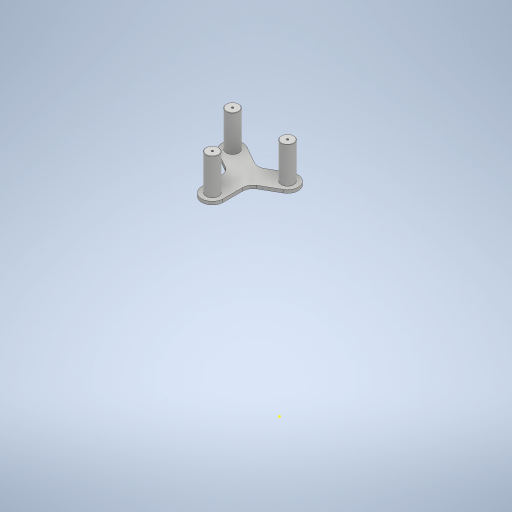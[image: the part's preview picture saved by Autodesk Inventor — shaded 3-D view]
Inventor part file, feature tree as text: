
AUTODESK INVENTOR PART (.ipt)
format: ipt  version: 2023 (Build 270158000, 158)  size: 316,416 bytes
history: native  units: mm
features: extrude x3, sketch x3, hole x3, plane x2, fillet x1
ambient origin geometry x8: Origin, YZ Plane, XZ Plane, XY Plane, X Axis, Y Axis, Z Axis, Center Point
bodies: 实体1 (feature_tree)
feature tree (12):
  plane  "工作平面5"
  extrude  "拉伸1"  Depth=12.0mm
  plane  "工作平面2"
  sketch  "草图9"  dims[d37=20.0mm d38=20.0mm]
  extrude  "拉伸3"  Depth=20.0mm
  hole  "孔4"  [1 undecoded]
  hole  "孔5"  [1 undecoded]
  hole  "孔6"  [1 undecoded]
  fillet  "圆角4"  Radius=37.0mm
  extrude  "拉伸4"  Depth=10.0mm
  sketch  "草图5"  dims[d31=12.0mm d33=12.0mm]
  sketch  "草图10"  dims[d39=15.0mm d44=10.0mm d45=3.0mm d46=0.0mm d87=12.0mm d88=37.0mm d91=0.0mm d101=10.0mm d102=10.0mm d94=1.941mm d95=5.029mm d96=4.0mm d97=2.0mm d98=90.0deg d99=10.0mm d100=20.594885mm d103=10.0mm d104=10.0mm d105=1.941mm d106=5.029mm d107=4.0mm d108=2.0mm d109=90.0deg d110=10.0mm d111=20.594885mm d112=10.0mm d113=10.0mm d114=1.941mm d115=5.029mm d116=4.0mm d117=2.0mm d118=90.0deg d119=10.0mm d120=20.594885mm d121=0.3mm d122=1.0mm d123=0.0mm]
note: 3 required parameter values undecoded (feature->parameter linkage not recoverable at this tier; creation-order binding heuristic only, values carry confidence <= 0.55)
